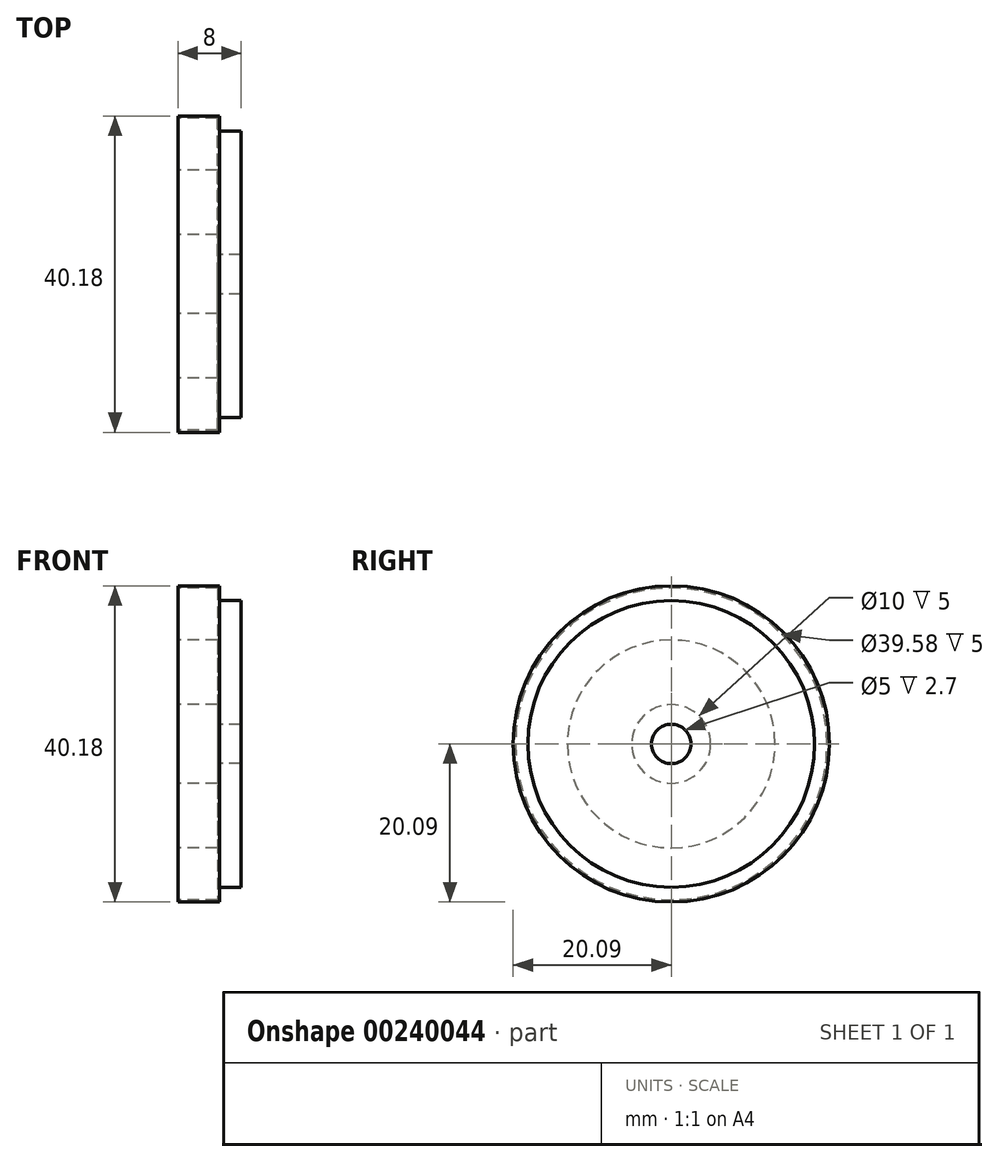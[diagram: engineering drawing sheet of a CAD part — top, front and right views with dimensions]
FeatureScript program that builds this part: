
annotation { "Feature Type Name" : "Feature", "Feature Type Description" : "" }
export const myFeature = defineFeature(function(context is Context, id is Id, definition is map)
    precondition{}
    {
        {
            var Q0;
            Q0=qCreatedBy(makeId("Top.planeOp"),FACE);
            var sketch = newSketch(context, id + "F0", { "sketchPlane" : qUnion([Q0])});
            skLineSegment(sketch, "E0", {"start": v(0, 5) * mm, "end": v(0, 13.2) * mm});
            skLineSegment(sketch, "E1", {"start": v(0, 13.2) * mm, "end": v(5, 13.2) * mm});
            skLineSegment(sketch, "E2", {"start": v(5, 13.2) * mm, "end": v(5, 18.2) * mm});
            skLineSegment(sketch, "E3", {"start": v(5, 18.2) * mm, "end": v(8, 18.2) * mm});
            skLineSegment(sketch, "E4", {"start": v(8, 18.2) * mm, "end": v(8, 2.5) * mm});
            skLineSegment(sketch, "E5", {"start": v(8, 2.5) * mm, "end": v(5, 2.5) * mm});
            skLineSegment(sketch, "E6", {"start": v(5, 2.5) * mm, "end": v(5, 5) * mm});
            skLineSegment(sketch, "E7", {"start": v(5, 5) * mm, "end": v(0, 5) * mm});
            skLineSegment(sketch, "E8", {"start": v(0, 0) * mm, "end": v(18.86, 0) * mm, "construction": true});
            skSolve(sketch);
        }
        {
            var Q0;
            Q0=qCreatedBy(makeId("Top.planeOp"),FACE);
            var sketch = newSketch(context, id + "F1", { "sketchPlane" : qUnion([Q0])});
            skLineSegment(sketch, "E9.bottom", {"start": v(5, 2.5) * mm, "end": v(5.3, 2.5) * mm});
            skLineSegment(sketch, "E9.top", {"start": v(5, 0) * mm, "end": v(5.3, 0) * mm});
            skLineSegment(sketch, "E9.left", {"start": v(5, 2.5) * mm, "end": v(5, 0) * mm});
            skLineSegment(sketch, "E9.right", {"start": v(5.3, 2.5) * mm, "end": v(5.3, 0) * mm});
            skLineSegment(sketch, "E10.top", {"start": v(5, 18.2) * mm, "end": v(5.3, 18.2) * mm});
            skLineSegment(sketch, "E10.left", {"start": v(5, 19.8) * mm, "end": v(5, 18.2) * mm});
            skLineSegment(sketch, "E10.right", {"start": v(5.3, 20.1) * mm, "end": v(5.3, 18.2) * mm});
            skLineSegment(sketch, "E11", {"start": v(5, 19.8) * mm, "end": v(0, 19.8) * mm});
            skLineSegment(sketch, "E12", {"start": v(0, 19.8) * mm, "end": v(0, 20.1) * mm});
            skLineSegment(sketch, "E13", {"start": v(0, 20.1) * mm, "end": v(5.3, 20.1) * mm});
            skSolve(sketch);
        }
        {
            var Q0;
            Q0=qCreatedBy(makeId("Top.planeOp"),FACE);
            var sketch = newSketch(context, id + "F2", { "sketchPlane" : qUnion([Q0])});
            skLineSegment(sketch, "E14.bottom", {"start": v(0, 18.2) * mm, "end": v(4.85, 18.2) * mm});
            skLineSegment(sketch, "E14.top", {"start": v(0, 13.6) * mm, "end": v(4.85, 13.6) * mm});
            skLineSegment(sketch, "E14.left", {"start": v(0, 18.2) * mm, "end": v(0, 13.6) * mm});
            skLineSegment(sketch, "E14.right", {"start": v(4.85, 18.2) * mm, "end": v(4.85, 13.6) * mm});
            skLineSegment(sketch, "E15.bottom", {"start": v(0, 2.5) * mm, "end": v(4.85, 2.5) * mm});
            skLineSegment(sketch, "E15.top", {"start": v(0, 4.6) * mm, "end": v(4.85, 4.6) * mm});
            skLineSegment(sketch, "E15.left", {"start": v(0, 2.5) * mm, "end": v(0, 4.6) * mm});
            skLineSegment(sketch, "E15.right", {"start": v(4.85, 2.5) * mm, "end": v(4.85, 4.6) * mm});
            skSolve(sketch);
        }
        {
            var Q0;
            Q0 = qSketchRegion(id + "F0", true);
            var Q1;
            Q1=sQuery(id+"F0.wireOp",EDGE,"E8");
            revolve(context, id + "F3", {"entities" : qUnion([Q0]), "axis" : qUnion([Q1]), "revolveType" : RevolveType.FULL});
        }
        {
            var Q0;
            Q0 = qSketchRegion(id + "F1", true);
            var Q1;
            Q1=sQuery(id+"F0.wireOp",EDGE,"E8");
            revolve(context, id + "F4", {"operationType" : NewBodyOperationType.ADD, "entities" : qUnion([Q0]), "axis" : qUnion([Q1]), "revolveType" : RevolveType.FULL});
        }
    });
